# Revit family: BIMLIB_Коллектор_802_3_РОСТерм
name_source: partatom
category: Оборудование
revit_build: Autodesk Revit 2017 (Build: 20170118_1100(x64)
units: mm (PartAtom-declared; Revit-internal decimal feet)

## family parameters
Всегда вертикально = Да
На основе рабочей плоскости = Нет
Общий = Нет
При загрузке вырезать с полостями = Нет
Размер круглого соединителя = Использовать диаметр
Тип детали = Нормальный
Точка расчета площади = Нет

## types (1)
- Коллекторная группа HEIZEN 802 для систем напольного отопления Ду32 на 3 выхода
    ADSK_URL документации изделия = http://rostherm.ru
    ADSK_URL страницы изделия = http://rostherm.ru
    ADSK_Версия Revit = 2017
    ADSK_Единица измерения = шт.
    ADSK_Завод-изготовитель = Heizen
    ADSK_Код изделия = 802-32-05-03
    ADSK_Марка = HEIZEN 802
    ADSK_Масса = 0
    ADSK_Материал = BIMLIB_Cталь_РТ
    ADSK_Наименование = Коллекторная группа HEIZEN 802 для систем напольного отопления Ду32 на 3 выхода
    ADSK_Наименование краткое = HEIZEN 802 Ду32 на 3 выхода
    ADSK_Обозначение = ГОСТ 12.2.063-2015
    BL_BIM library = https://bimlib.pro
    URL = http://rostherm.ru
    Изготовитель = РОСТерм
    Описание = Коллекторная группа для систем напольного отопления
    РТ_DN1 = 32 мм
    РТ_DN2 = 20 мм
    РТ_DN3 = 15 мм
    РТ_R/2 = 10 мм
    РТ_R1 = 16 мм

## geometry (parser evidence)
native form markers: Sweep x1
no freeform markers — native parametric forms only
